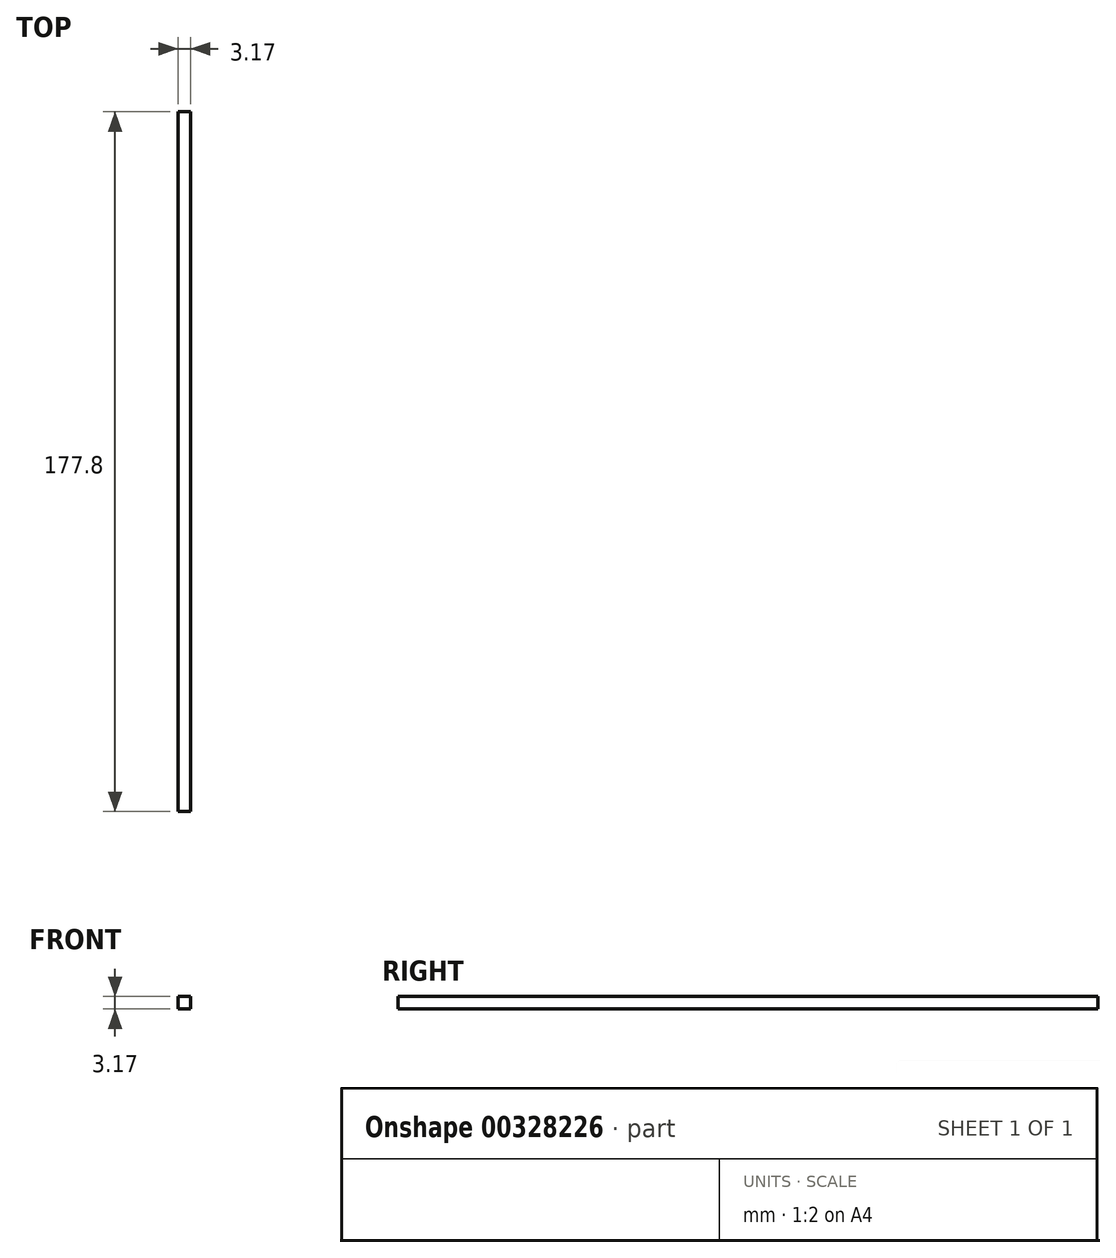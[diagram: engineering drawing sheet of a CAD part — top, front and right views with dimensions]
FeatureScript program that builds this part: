
annotation { "Feature Type Name" : "Feature", "Feature Type Description" : "" }
export const myFeature = defineFeature(function(context is Context, id is Id, definition is map)
    precondition{}
    {
        {
            var Q0;
            Q0=qCreatedBy(makeId("Top.planeOp"),FACE);
            var sketch = newSketch(context, id + "F0", { "sketchPlane" : qUnion([Q0])});
            skLineSegment(sketch, "E0", {"start": v(0, 0) * mm, "end": v(0, 177.8) * mm});
            skLineSegment(sketch, "E1", {"start": v(0, 177.8) * mm, "end": v(-3.18, 177.8) * mm});
            skLineSegment(sketch, "E2", {"start": v(-3.18, 177.8) * mm, "end": v(-3.17, 0) * mm});
            skLineSegment(sketch, "E3", {"start": v(-3.17, 0) * mm, "end": v(0, 0) * mm});
            skSolve(sketch);
        }
        {
            var Q0;
            Q0=makeQuery(id+"F0.imprint","IMPRINT",FACE,{"disambiguationData":[TD([[makeQuery(id+"F0.imprint","IMPRINT",EDGE,{"derivedFrom":sQuery(id+"F0.wireOp",EDGE,"E0")}),1.0]])]});
            extrude(context, id + "F1", {"entities" : qUnion([Q0]), "depth" : 3.17 * mm});
        }
    });
